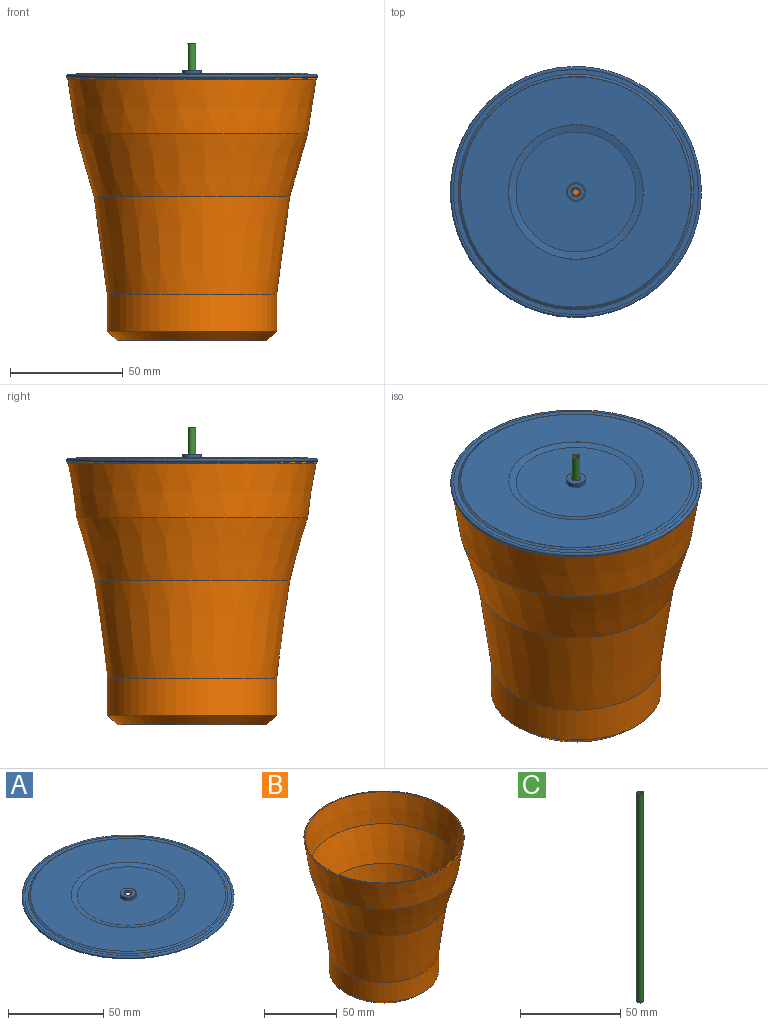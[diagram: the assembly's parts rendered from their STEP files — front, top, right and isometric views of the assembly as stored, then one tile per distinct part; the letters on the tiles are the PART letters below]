
ASSEMBLY  parts=3 mates=2
PART A: 18 faces, bbox 120.4x120.4x3.5 mm
  f0: plane 7.35x7.35mm, normal (0,0,-1), area 28.5mm2, adj f1,f17
  f1: cylinder r=3.67mm len=7.35mm, axis (0,0,1), area 47.7mm2, adj f0,f2
  f2: plane 53.25x53.25mm, normal (0,0,-1), area 2184.3mm2, adj f1,f3
  f3: cone r=26.62mm half-angle=77.6deg, axis (0,0,1), area 581.7mm2, adj f2,f4
  f4: plane 102.01x102.01mm, normal (0,0,-1), area 5378.2mm2, adj f3,f5
  f5: cone r=51.01mm half-angle=56deg, axis (0,0,-1), area 409.2mm2, adj f4,f6
  f6: cone r=52.05mm half-angle=89.9deg, axis (0,0,1), area 825.4mm2, adj f5,f7
  f7: torus R=54.79mm, axis (0,0,1), area 420.5mm2, adj f6,f8
  f8: cylinder r=54.86mm len=109.71mm, axis (0,0,1), area 177.1mm2, adj f7,f9
  f9: torus R=54.79mm, axis (0,0,1), area 1061.9mm2, adj f8,f10
  f10: cone r=52.21mm half-angle=89.9deg, axis (0,0,1), area 685.4mm2, adj f9,f11
  f11: cone r=51.16mm half-angle=56deg, axis (0,0,-1), area 410.3mm2, adj f10,f12
  f12: plane 102.32x102.32mm, normal (0,0,1), area 5438.3mm2, adj f11,f13
  f13: cone r=26.57mm half-angle=77.6deg, axis (0,0,1), area 580.6mm2, adj f12,f14
  f14: plane 53.14x53.14mm, normal (0,0,1), area 2162.5mm2, adj f13,f15
  f15: cylinder r=4.18mm len=8.36mm, axis (0,0,1), area 54.3mm2, adj f14,f16
  f16: plane 8.36x8.36mm, normal (0,0,1), area 41mm2, adj f15,f17
  f17: cylinder r=2.11mm len=4.21mm, axis (0,0,1), area 6.7mm2, adj f0,f16
PART B: 17 faces, bbox 119.3x119.3x116.3 mm
  f0: plane 66.13x66.13mm, normal (0,0,-1), area 1781.5mm2, adj f1,f16
  f1: cone r=33.06mm half-angle=48deg, axis (0,0,1), area 1335.9mm2, adj f0,f2
  f2: cylinder r=37.54mm len=75.08mm, axis (0,0,1), area 3878.4mm2, adj f1,f3
  f3: cone r=37.54mm half-angle=7.7deg, axis (0,0,1), area 11086.5mm2, adj f2,f4
  f4: cone r=43.36mm half-angle=15.8deg, axis (0,0,1), area 8618.5mm2, adj f3,f5
  f5: cone r=51.27mm half-angle=8.8deg, axis (0,0,1), area 8170.6mm2, adj f4,f6
  f6: torus R=54.79mm, axis (0,0,1), area 434.9mm2, adj f5,f7
  f7: cone r=50.77mm half-angle=8.8deg, axis (0,0,1), area 8083.5mm2, adj f6,f8
  f8: cone r=42.86mm half-angle=15.8deg, axis (0,0,1), area 8529.3mm2, adj f7,f9
  f9: cone r=37.03mm half-angle=7.7deg, axis (0,0,1), area 10966.2mm2, adj f8,f10
  f10: cylinder r=37.03mm len=74.06mm, axis (0,0,1), area 3781.2mm2, adj f9,f11
  f11: cone r=32.87mm half-angle=48deg, axis (0,0,1), area 1230.1mm2, adj f10,f12
  f12: plane 65.74x65.74mm, normal (0,0,1), area 1712.9mm2, adj f11,f13
  f13: cone r=18.97mm half-angle=48deg, axis (0,0,-1), area 740.9mm2, adj f12,f14
  f14: plane 37.94x37.94mm, normal (0,0,1), area 1130.4mm2, adj f13
  f15: plane 37.55x37.55mm, normal (0,0,-1), area 1107.3mm2, adj f16
  f16: cone r=18.77mm half-angle=48deg, axis (0,0,-1), area 734mm2, adj f0,f15
PART C: 8 faces, bbox 3.8x3.8x127 mm
  f0: torus R=1.72mm, axis (0,0,1), area 0.4mm2, adj f1,f7
  f1: cylinder r=1.74mm len=126.95mm, axis (0,0,1), area 1390.3mm2, adj f0,f2
  f2: torus R=1.72mm, axis (0,0,1), area 0.4mm2, adj f1,f3
  f3: plane 3.44x3.44mm, normal (0,0,-1), area 1.5mm2, adj f2,f4
  f4: torus R=1.57mm, axis (0,0,1), area 0.4mm2, adj f3,f5
  f5: cylinder r=1.55mm len=126.95mm, axis (0,0,1), area 1235.9mm2, adj f4,f6
  f6: torus R=1.57mm, axis (0,0,1), area 0.4mm2, adj f5,f7
  f7: plane 3.44x3.44mm, normal (0,0,1), area 1.5mm2, adj f0,f6
PLACE A t=(-3.24,-10.95,51.59)mm
PLACE B t=(-3.24,-10.95,-21.29)mm fixed
PLACE C t=(-3.24,-10.95,-12.53)mm
MATE slider A.f1 <-> B.f1  axis (0,0,1) through (-3.24,-10.95,61.98)mm
MATE slider C.f0 <-> B.f1  axis (0,0,1) through (-3.24,-10.95,77.35)mm
